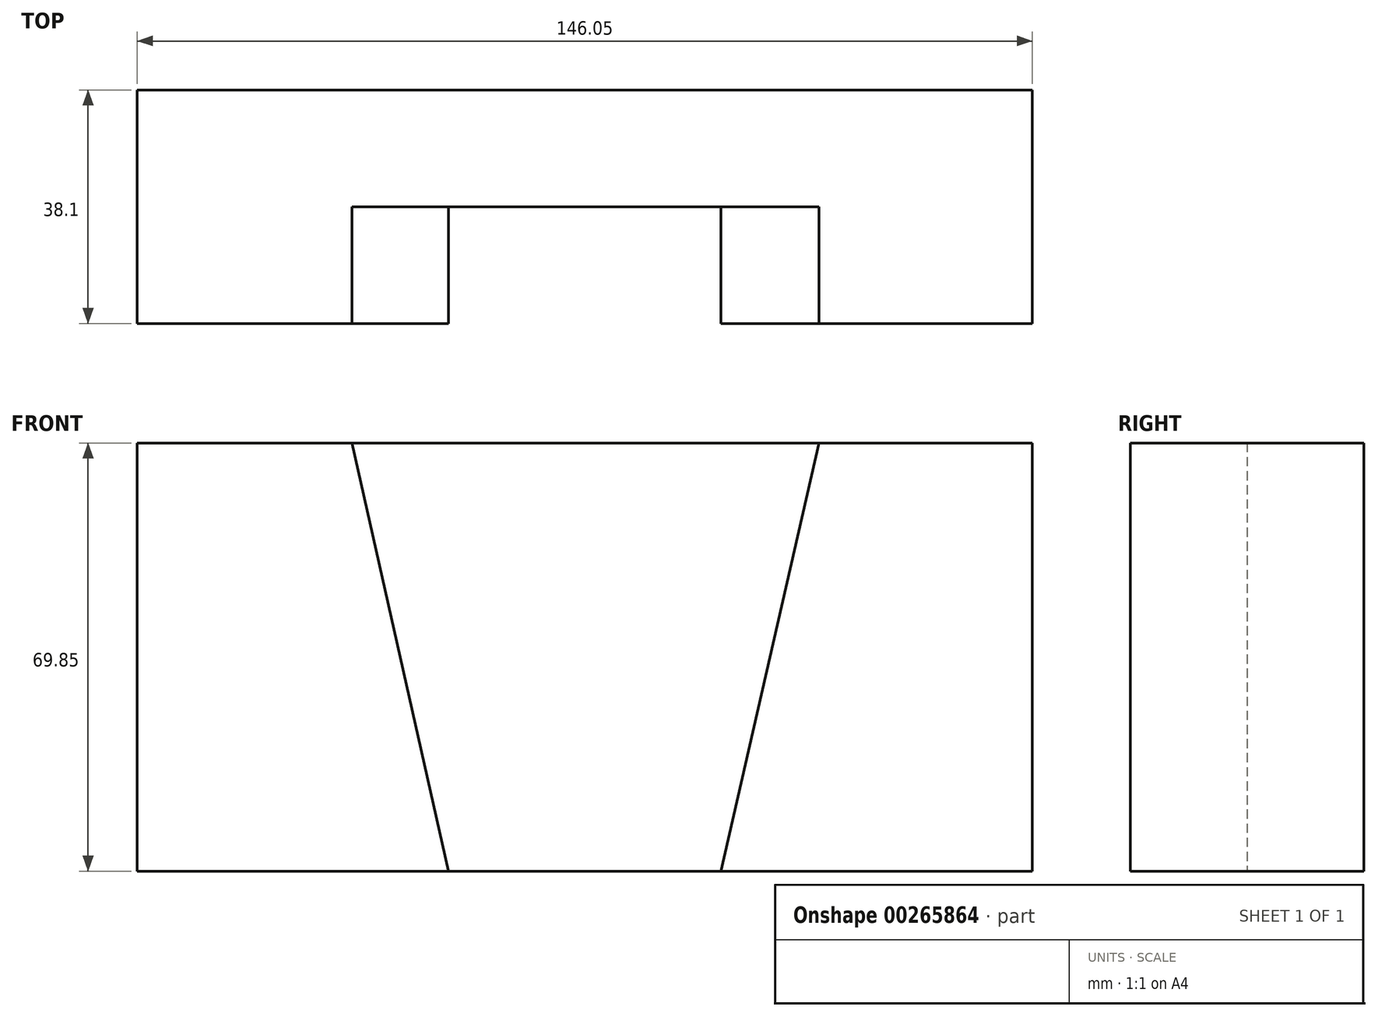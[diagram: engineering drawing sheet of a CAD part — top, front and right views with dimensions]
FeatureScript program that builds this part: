
annotation { "Feature Type Name" : "Feature", "Feature Type Description" : "" }
export const myFeature = defineFeature(function(context is Context, id is Id, definition is map)
    precondition{}
    {
        {
            var Q0;
            Q0=qCreatedBy(makeId("Front.planeOp"),FACE);
            var sketch = newSketch(context, id + "F0", { "sketchPlane" : qUnion([Q0])});
            skLineSegment(sketch, "E0.bottom", {"start": v(-72.79, 27.52) * mm, "end": v(73.26, 27.52) * mm});
            skLineSegment(sketch, "E0.top", {"start": v(-72.79, -42.33) * mm, "end": v(73.26, -42.33) * mm});
            skLineSegment(sketch, "E0.left", {"start": v(-72.79, 27.52) * mm, "end": v(-72.79, -42.33) * mm});
            skLineSegment(sketch, "E0.right", {"start": v(73.26, 27.52) * mm, "end": v(73.26, -42.33) * mm});
            skSolve(sketch);
        }
        {
            var Q0;
            Q0 = qSketchRegion(id + "F0", true);
            extrude(context, id + "F1", {"entities" : qUnion([Q0]), "depth" : 38.1 * mm});
        }
        {
            var Q0;
            Q0=makeQuery(id+"F1.opExtrude","CAP_FACE",FACE,{"disambiguationData":[OSD([sQuery(id+"F0.wireOp",EDGE,"E0.bottom"),sQuery(id+"F0.wireOp",EDGE,"E0.top"),sQuery(id+"F0.wireOp",EDGE,"E0.left"),sQuery(id+"F0.wireOp",EDGE,"E0.right")])],"isStart":false});
            var sketch = newSketch(context, id + "F2", { "sketchPlane" : qUnion([Q0])});
            skLineSegment(sketch, "E1", {"start": v(-37.73, 27.52) * mm, "end": v(38.47, 27.52) * mm});
            skLineSegment(sketch, "E2", {"start": v(22.46, -42.33) * mm, "end": v(-21.99, -42.33) * mm});
            skLineSegment(sketch, "E3", {"start": v(-37.73, 27.52) * mm, "end": v(-21.99, -42.33) * mm});
            skLineSegment(sketch, "E4", {"start": v(38.47, 27.52) * mm, "end": v(22.46, -42.33) * mm});
            skSolve(sketch);
        }
        {
            var Q0;
            Q0=makeQuery(id+"F2.imprint","IMPRINT",FACE,{"disambiguationData":[TD([[makeQuery(id+"F2.imprint","IMPRINT",EDGE,{"derivedFrom":sQuery(id+"F2.wireOp",EDGE,"E1")}),-1.0]])]});
            extrude(context, id + "F3", {"entities" : qUnion([Q0]), "operationType" : NewBodyOperationType.REMOVE, "oppositeDirection" : true, "depth" : 19.05 * mm});
        }
    });
